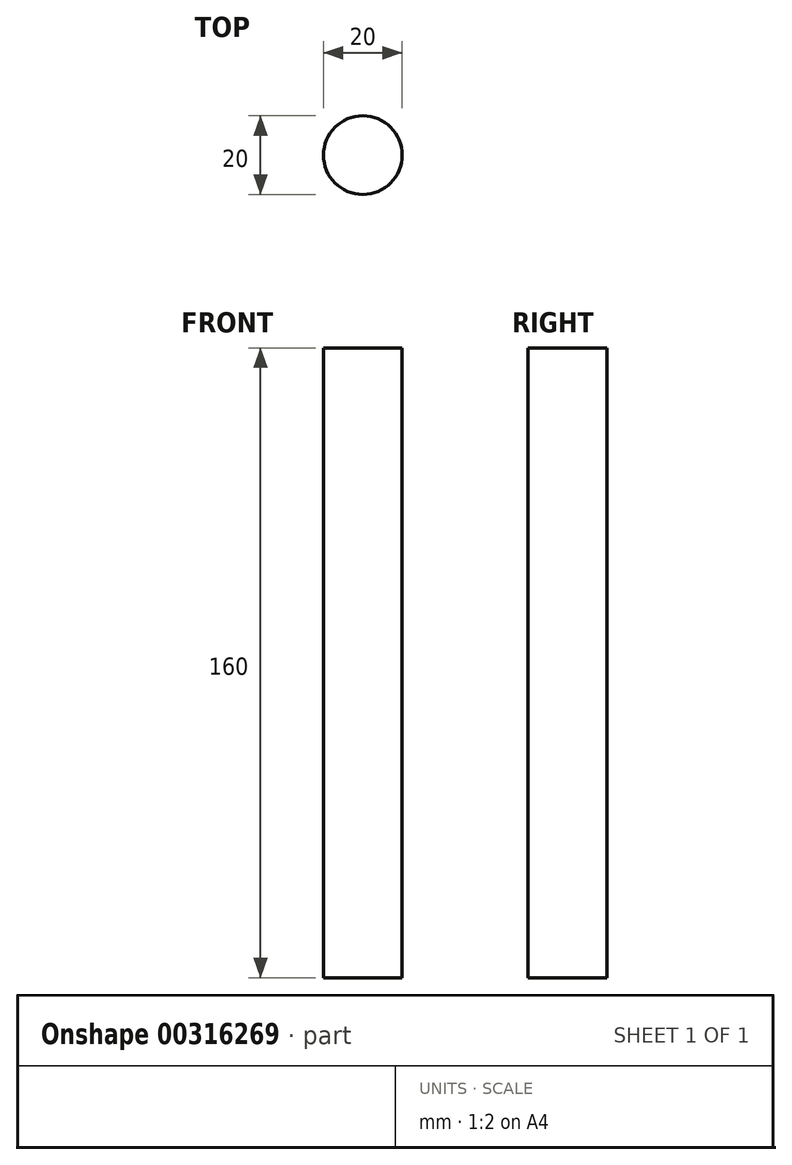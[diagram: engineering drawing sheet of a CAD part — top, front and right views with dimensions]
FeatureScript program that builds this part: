
annotation { "Feature Type Name" : "Feature", "Feature Type Description" : "" }
export const myFeature = defineFeature(function(context is Context, id is Id, definition is map)
    precondition{}
    {
        {
            var Q0;
            Q0=qCreatedBy(makeId("Top.planeOp"),FACE);
            var sketch = newSketch(context, id + "F0", { "sketchPlane" : qUnion([Q0])});
            skCircle(sketch, "E0", {"center": v(0, 0) * mm, "radius": 10 * mm});
            skSolve(sketch);
        }
        {
            var Q0;
            Q0 = qSketchRegion(id + "F0", true);
            extrude(context, id + "F1", {"entities" : qUnion([Q0]), "endBound" : BoundingType.SYMMETRIC, "depth" : 160 * mm});
        }
    });
